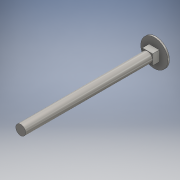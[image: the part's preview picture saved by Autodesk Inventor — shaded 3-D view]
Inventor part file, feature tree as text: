
AUTODESK INVENTOR PART (.ipt)
format: ipt  version: 2016 (Build 200138000, 138)  size: 124,416 bytes
history: native  units: mm
features: sketch x3, extrude x2, revolve x1
ambient origin geometry x8: Origin, YZ Plane, XZ Plane, XY Plane, X Axis, Y Axis, Z Axis, Center Point
bodies: Body1 (feature_tree)
feature tree (6):
  revolve  "Revolution1"  [1 undecoded]
  extrude  "Extrusion2"  TaperAngle=180.0deg  [1 undecoded]
  extrude  "Extrusion3"  Depth=6.1mm
  sketch  "Sketch4"  dims[d7=3.0mm d8=8.05mm]
  sketch  "Sketch5"  dims[d9=1.0mm d10=180.0deg]
  sketch  "Sketch6"  dims[d11=6.1mm d12=6.1mm d13=3.05mm d14=3.05mm d15=4.0mm d16=0.0mm d17=5.89mm d18=75.5mm d19=0.0mm]
note: 2 required parameter values undecoded (feature->parameter linkage not recoverable at this tier; creation-order binding heuristic only, values carry confidence <= 0.55)